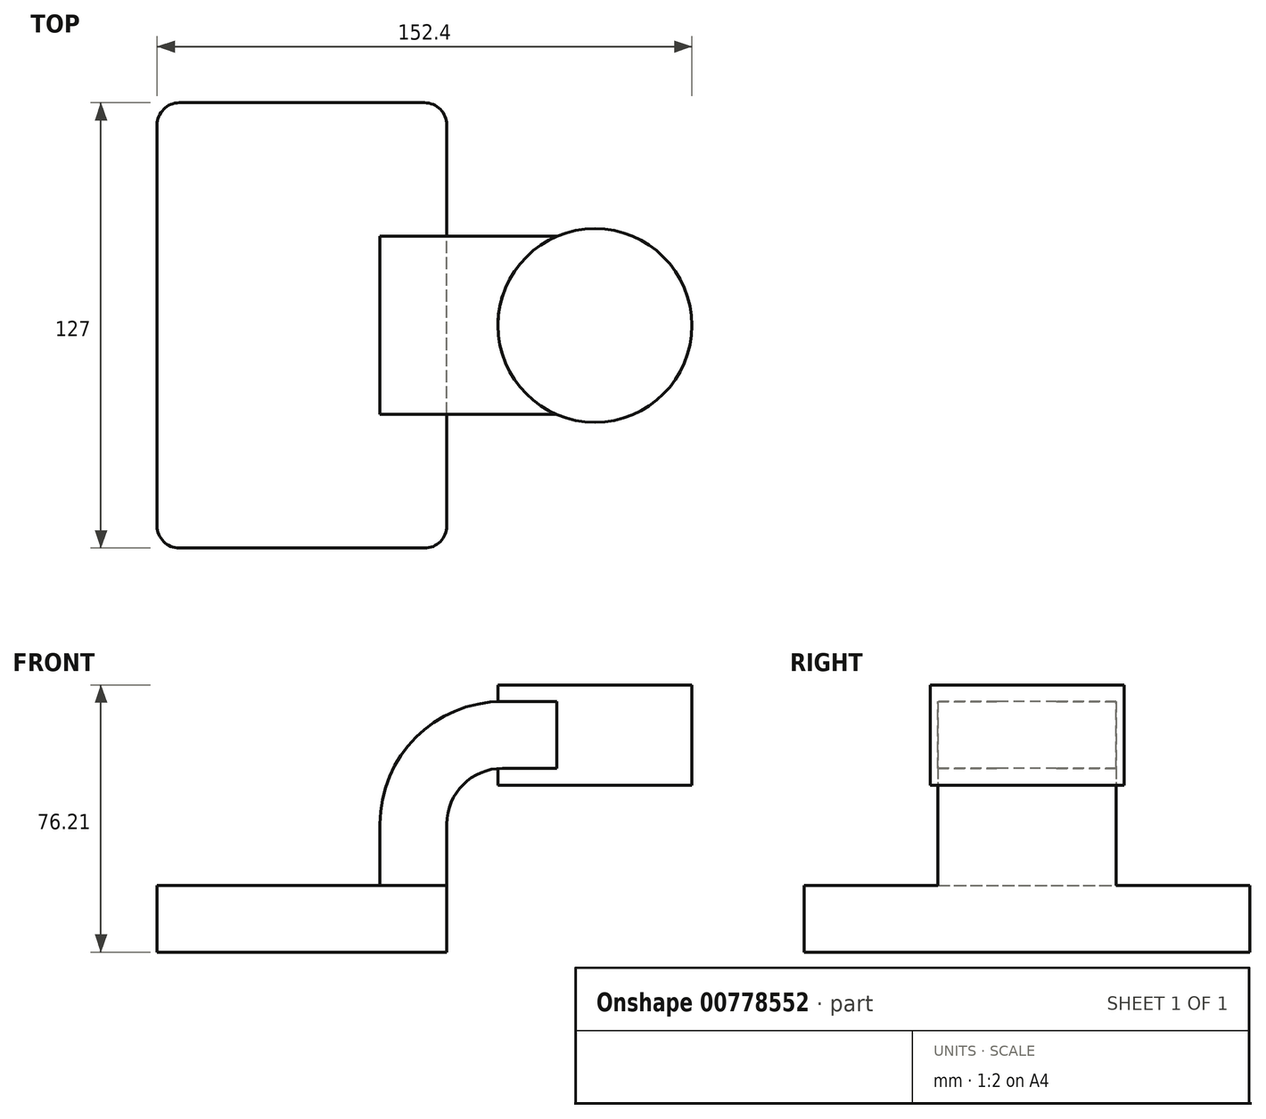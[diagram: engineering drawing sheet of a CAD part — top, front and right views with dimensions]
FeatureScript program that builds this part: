
annotation { "Feature Type Name" : "Feature", "Feature Type Description" : "" }
export const myFeature = defineFeature(function(context is Context, id is Id, definition is map)
    precondition{}
    {
        {
            var Q0;
            Q0=qCreatedBy(makeId("Front.planeOp"),FACE);
            var sketch = newSketch(context, id + "F0", { "sketchPlane" : qUnion([Q0])});
            skLineSegment(sketch, "E0.bottom", {"start": v(-41.27, -9.53) * mm, "end": v(41.28, -9.53) * mm});
            skLineSegment(sketch, "E0.top", {"start": v(-41.28, 9.52) * mm, "end": v(41.28, 9.52) * mm});
            skLineSegment(sketch, "E0.left", {"start": v(-41.28, -9.53) * mm, "end": v(-41.28, 9.53) * mm});
            skLineSegment(sketch, "E0.right", {"start": v(41.28, -9.53) * mm, "end": v(41.28, 9.52) * mm});
            skPoint(sketch, "E0.middle", {"position": v(0, 0) * mm});
            skLineSegment(sketch, "E1.bottom", {"start": v(111.13, 38.1) * mm, "end": v(60.33, 38.1) * mm});
            skLineSegment(sketch, "E1.top", {"start": v(111.13, 66.67) * mm, "end": v(60.33, 66.67) * mm});
            skLineSegment(sketch, "E1.left", {"start": v(111.13, 38.1) * mm, "end": v(111.13, 66.68) * mm});
            skLineSegment(sketch, "E1.right", {"start": v(60.33, 38.1) * mm, "end": v(60.33, 66.68) * mm});
            skPoint(sketch, "E1.middle", {"position": v(85.73, 52.39) * mm});
            skLineSegment(sketch, "E2", {"start": v(41.28, 9.52) * mm, "end": v(41.28, 27) * mm});
            skArc(sketch, "E3", {"start": v(41.27, 27) * mm, "mid": v(45.92, 38.23) * mm, "end": v(57.15, 42.88) * mm});
            skLineSegment(sketch, "E4", {"start": v(57.15, 42.88) * mm, "end": v(83.48, 42.88) * mm});
            skLineSegment(sketch, "E5.0", {"start": v(57.15, 61.93) * mm, "end": v(83.48, 61.93) * mm});
            skArc(sketch, "E5.1", {"start": v(22.23, 27) * mm, "mid": v(32.45, 51.7) * mm, "end": v(57.15, 61.93) * mm});
            skLineSegment(sketch, "E5.2", {"start": v(22.22, 9.52) * mm, "end": v(22.22, 27) * mm});
            skLineSegment(sketch, "E6", {"start": v(83.48, 42.88) * mm, "end": v(83.48, 61.93) * mm});
            skLineSegment(sketch, "E7", {"start": v(83.48, 66.67) * mm, "end": v(83.48, 38.1) * mm});
            skFitSpline(sketch, "E8", {"points": [v(-41.27, 9.53) * mm, v(57.15, 61.93) * mm], "startDerivative": vector(0.28, 105.61) * mm, "endDerivative": vector(121.4, -4.06) * mm});
            skSolve(sketch);
        }
        {
            var Q0;
            Q0=makeQuery(id+"F0.imprint","IMPRINT",FACE,{"disambiguationData":[TD([[makeQuery(id+"F0.imprint","IMPRINT",EDGE,{"derivedFrom":sQuery(id+"F0.wireOp",EDGE,"E0.bottom")}),1.0]])]});
            extrude(context, id + "F1", {"entities" : qUnion([Q0]), "endBound" : BoundingType.SYMMETRIC, "depth" : 127 * mm, "offsetDistance" : 25.4 * mm});
        }
        {
            var Q0;
            {var subQ1=sQuery(id+"F0.wireOp",EDGE,"E2");Q0=makeQuery(id+"F0.imprint","IMPRINT",FACE,{"disambiguationData":[TD([[makeQuery(id+"F0.imprint","IMPRINT",EDGE,{"derivedFrom":subQ1}),1.0]])]});}
            extrude(context, id + "F2", {"entities" : qUnion([Q0]), "operationType" : NewBodyOperationType.ADD, "endBound" : BoundingType.SYMMETRIC, "depth" : 50.8 * mm, "offsetDistance" : 25.4 * mm});
        }
        {
            var Q0;
            {var subQ0=sQuery(id+"F0.wireOp",EDGE,"E4");var subQ1=sQuery(id+"F0.wireOp",EDGE,"E1.right");var subQ2=makeQuery(id+"F0.imprint","INTERSECT",VERTEX,{"derivedFrom":[subQ1,subQ0]});Q0=makeQuery(id+"F0.imprint","IMPRINT",FACE,{"disambiguationData":[TD([[makeQuery(id+"F0.imprint","IMPRINT",EDGE,{"disambiguationData":[TD([[subQ2,-1.0]])],"derivedFrom":subQ1}),-1.0]])]});}
            extrude(context, id + "F3", {"entities" : qUnion([Q0]), "operationType" : NewBodyOperationType.ADD, "endBound" : BoundingType.SYMMETRIC, "depth" : 50.8 * mm, "offsetDistance" : 25.4 * mm});
        }
        {
            var Q0;
            Q0=makeQuery(id+"F0.imprint","IMPRINT",FACE,{"disambiguationData":[TD([[makeQuery(id+"F0.imprint","IMPRINT",EDGE,{"derivedFrom":sQuery(id+"F0.wireOp",EDGE,"E5.1")}),1.0]])]});
            extrude(context, id + "F4", {"entities" : qUnion([Q0]), "operationType" : NewBodyOperationType.ADD, "endBound" : BoundingType.SYMMETRIC, "depth" : 15.88 * mm, "offsetDistance" : 25.4 * mm});
        }
        {
            var Q0;
            {var subQ4=sQuery(id+"F0.wireOp",EDGE,"E1.left");Q0=makeQuery(id+"F0.imprint","IMPRINT",FACE,{"disambiguationData":[TD([[makeQuery(id+"F0.imprint","IMPRINT",EDGE,{"derivedFrom":subQ4}),1.0]])]});}
            var Q1;
            Q1=sQuery(id+"F0.wireOp",EDGE,"E7");
            revolve(context, id + "F5", {"operationType" : NewBodyOperationType.ADD, "surfaceOperationType" : NewSurfaceOperationType.NEW, "entities" : qUnion([Q0]), "axis" : qUnion([Q1]), "revolveType" : RevolveType.FULL});
        }
        {
            var Q0;
            Q0=makeQuery(id+"F1.opExtrude","CAP_EDGE",EDGE,{"disambiguationData":[OSD([sQuery(id+"F0.wireOp",EDGE,"E0.left")])],"isStart":false});
            var Q1;
            Q1=makeQuery(id+"F1.opExtrude","CAP_EDGE",EDGE,{"disambiguationData":[OSD([sQuery(id+"F0.wireOp",EDGE,"E0.right")])],"isStart":false});
            var Q2;
            Q2=makeQuery(id+"F1.opExtrude","CAP_EDGE",EDGE,{"disambiguationData":[OSD([sQuery(id+"F0.wireOp",EDGE,"E0.right")])],"isStart":true});
            var Q3;
            Q3=makeQuery(id+"F1.opExtrude","CAP_EDGE",EDGE,{"disambiguationData":[OSD([sQuery(id+"F0.wireOp",EDGE,"E0.left")])],"isStart":true});
            fillet(context, id + "F6", {"entities" : qUnion([Q0, Q1, Q2, Q3]), "radius" : 6.35 * mm, "tangentPropagation" : true, "allowEdgeOverflow" : false});
        }
    });
